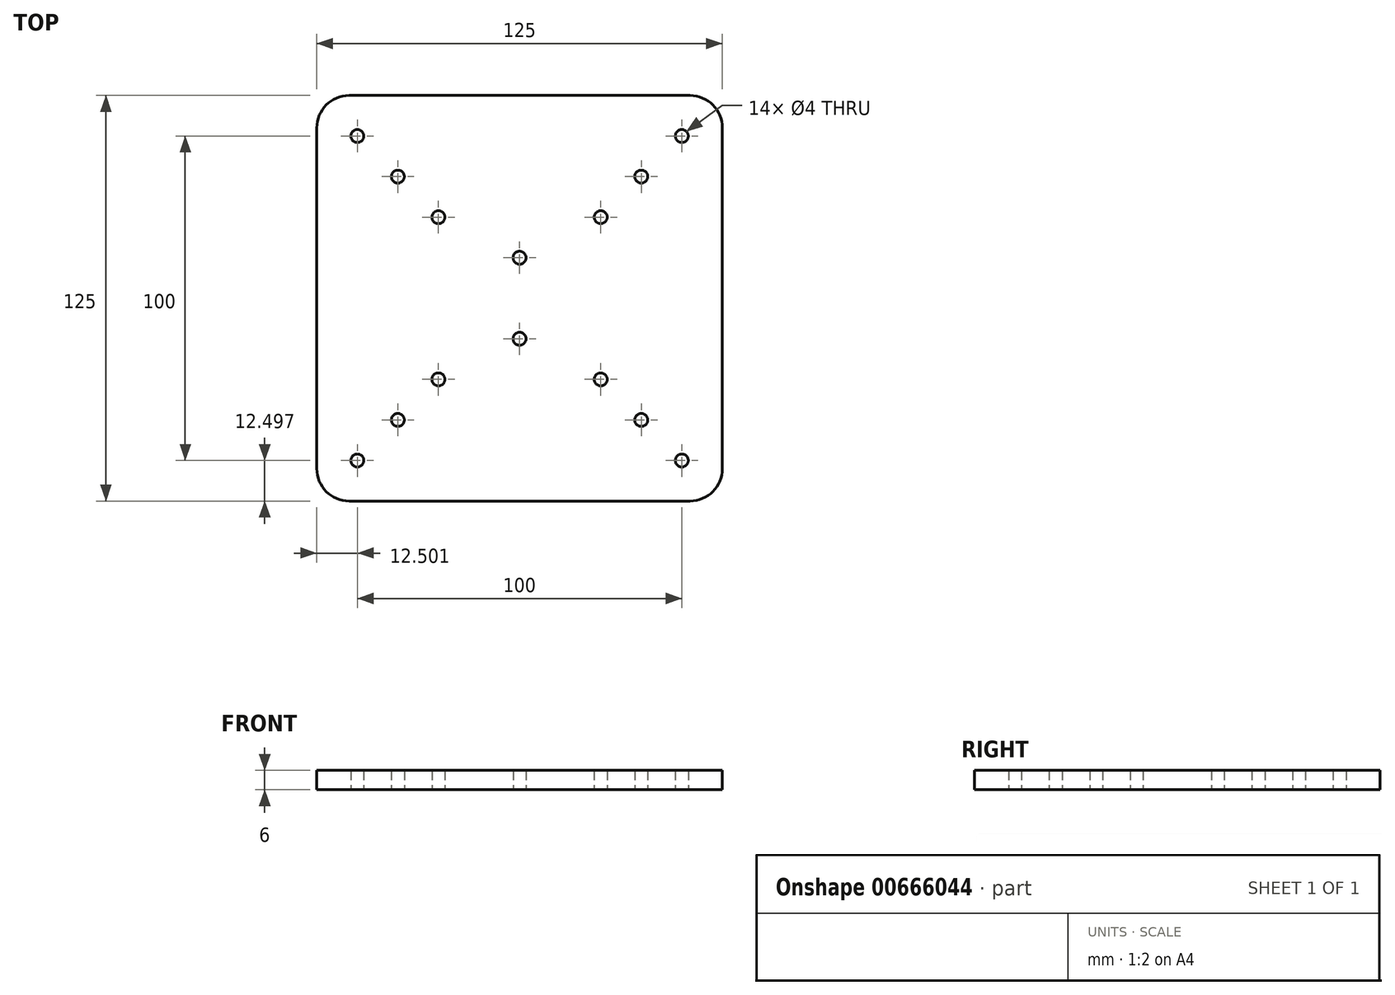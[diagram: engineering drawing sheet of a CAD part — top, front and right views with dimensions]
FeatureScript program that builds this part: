
annotation { "Feature Type Name" : "Feature", "Feature Type Description" : "" }
export const myFeature = defineFeature(function(context is Context, id is Id, definition is map)
    precondition{}
    {
        {
            var Q0;
            Q0=qCreatedBy(makeId("Top.planeOp"),FACE);
            var sketch = newSketch(context, id + "F0", { "sketchPlane" : qUnion([Q0])});
            skLineSegment(sketch, "E0.bottom", {"start": v(-54.27, 76.18) * mm, "end": v(70.73, 76.18) * mm});
            skLineSegment(sketch, "E0.top", {"start": v(-54.27, -48.82) * mm, "end": v(70.73, -48.82) * mm});
            skLineSegment(sketch, "E0.left", {"start": v(-54.27, 76.18) * mm, "end": v(-54.27, -48.82) * mm});
            skLineSegment(sketch, "E0.right", {"start": v(70.73, 76.18) * mm, "end": v(70.73, -48.82) * mm});
            skCircle(sketch, "E1", {"center": v(-41.77, -36.32) * mm, "radius": 2 * mm});
            skCircle(sketch, "E2", {"center": v(58.23, -36.32) * mm, "radius": 2 * mm});
            skCircle(sketch, "E3", {"center": v(-41.77, 63.68) * mm, "radius": 2 * mm});
            skCircle(sketch, "E4", {"center": v(58.23, 63.68) * mm, "radius": 2 * mm});
            skCircle(sketch, "E5", {"center": v(-29.27, -23.82) * mm, "radius": 2 * mm});
            skCircle(sketch, "E6", {"center": v(45.73, -23.82) * mm, "radius": 2 * mm});
            skCircle(sketch, "E7", {"center": v(-29.27, 51.18) * mm, "radius": 2 * mm});
            skCircle(sketch, "E8", {"center": v(45.73, 51.18) * mm, "radius": 2 * mm});
            skCircle(sketch, "E9", {"center": v(-16.77, 38.68) * mm, "radius": 2 * mm});
            skCircle(sketch, "E10", {"center": v(33.23, 38.68) * mm, "radius": 2 * mm});
            skCircle(sketch, "E11", {"center": v(-16.77, -11.32) * mm, "radius": 2 * mm});
            skCircle(sketch, "E12", {"center": v(33.23, -11.32) * mm, "radius": 2 * mm});
            skCircle(sketch, "E13", {"center": v(8.23, 1.18) * mm, "radius": 2 * mm});
            skCircle(sketch, "E14", {"center": v(8.23, 26.18) * mm, "radius": 2 * mm});
            skSolve(sketch);
        }
        {
            var Q0;
            Q0=qSketchRegion(id+"F0",true);
            extrude(context, id + "F1", {"entities" : qUnion([Q0]), "depth" : 6 * mm});
        }
        {
            var Q0;
            Q0=makeQuery(id+"F1.opExtrude","SWEPT_EDGE",EDGE,{"disambiguationData":[OSD([sQuery(id+"F0.wireOp",EDGE,"E0.bottom"),sQuery(id+"F0.wireOp",EDGE,"E0.left")])]});
            var Q1;
            Q1=makeQuery(id+"F1.opExtrude","SWEPT_EDGE",EDGE,{"disambiguationData":[OSD([sQuery(id+"F0.wireOp",EDGE,"E0.top"),sQuery(id+"F0.wireOp",EDGE,"E0.left")])]});
            var Q2;
            Q2=makeQuery(id+"F1.opExtrude","SWEPT_EDGE",EDGE,{"disambiguationData":[OSD([sQuery(id+"F0.wireOp",EDGE,"E0.top"),sQuery(id+"F0.wireOp",EDGE,"E0.right")])]});
            var Q3;
            Q3=makeQuery(id+"F1.opExtrude","SWEPT_EDGE",EDGE,{"disambiguationData":[OSD([sQuery(id+"F0.wireOp",EDGE,"E0.bottom"),sQuery(id+"F0.wireOp",EDGE,"E0.right")])]});
            fillet(context, id + "F2", {"entities" : qUnion([Q0, Q1, Q2, Q3]), "radius" : 10 * mm, "tangentPropagation" : true, "allowEdgeOverflow" : false});
        }
    });
